# Revit family: M_Valve_Balancing and Control_MEPcontent_Oventrop_Hydrocontrol VFC 10626 DN 200-400 PN16 DIN
name_source: partatom
category: Pipe Accessories
revit_build: Autodesk Revit 2015 (Build: 20140223_1515(x64)
units: mm (PartAtom-declared; Revit-internal decimal feet)

## types (5) — shared parameters
Angle = 60.00°
Angle 2 = 30.00°
Angle 3 = -60.00°
Article Description = Double regulating and commissioning valve
Article Type = Hydrocontrol VFC 10626 DN 200-400 PN16 DIN
Black = Color RGB 35-35-35
Bronze = Color RGB 156-122-90
Content Supplier URL = www.mepcontent.eu
Custom = No
Description = Double regulating and commissioning valve
EMCS Version = 2.0
ETIM Article Class = EC011463
Family Version = 10.14
Hb5 = 10 mm  [stored 0.0328084 ft]
Hlp1 = 56 mm  [stored 0.183727 ft]
IFCExportAs = IfcValveType
IFCExportType = PRESSUREREDUCING
Lgt1 = 2 mm  [stored 0.00656168 ft]
MEPcontent Class = VALVE_BALANCING
Manufacturer = Oventrop
Manufacturer URL = http://www.oventrop.de
Model = Hydrocontrol VFC 10626 DN 200-400 PN16 DIN
Pressure Drop = 0.0 Pa
Product Line = Oventrop
R1 = 9 mm  [stored 0.0295276 ft]
R2 = 10 mm  [stored 0.0328084 ft]
RegulatorRadius = 150 mm
Revit Version = 2015
Steel = Color RGB 140-140-140
URL = www.stabiplan.com
r1 = 2 mm  [stored 0.00656168 ft]
r2 = 3 mm  [stored 0.00984252 ft]

## per-type parameters (varying)
- DN 200: CurDst=67 mm; Dst1=68 mm; DstChk=68 mm; FlangeDiameter=340 mm; GTIN=4026755126174; H=473 mm; Hb1=460 mm; Hb2=290 mm; Hb3=48 mm; Hb4=110 mm; Hb6=218 mm; Height=467 mm; Hlp2=22 mm  [stored 0.0721785 ft]; K=295 mm; L2=67 mm; Length=600 mm; Lgt2=20 mm  [stored 0.0656168 ft]; Lgt3=59 mm; Lgt4=217 mm; Manufacturer Art. No.=1062656; NominalDiameter=200 mm; NominalRadius=100 mm; OuterDiameter=219 mm; Rad1=148 mm; Rad2=170 mm; Rad3=119 mm; Rad4=116 mm; Rad5=156 mm; Rad6=146 mm; Rad7=160 mm; VDst=54 mm; VHth=126 mm
- DN 250: CurDst=81 mm; Dst1=91 mm; DstChk=91 mm; FlangeDiameter=405 mm; GTIN=4026755180190; H=486 mm; Hb1=475 mm; Hb2=292 mm; Hb3=49 mm; Hb4=111 mm; Hb6=220 mm; Height=480 mm; Hlp2=27 mm; K=355 mm; L2=81 mm; Length=730 mm; Lgt2=22 mm  [stored 0.0721785 ft]; Lgt3=68 mm; Lgt4=260 mm; Manufacturer Art. No.=1062657; NominalDiameter=250 mm; NominalRadius=125 mm; OuterDiameter=273 mm; Rad1=178 mm; Rad2=203 mm; Rad3=143 mm; Rad4=140 mm; Rad5=180 mm; Rad6=170 mm; Rad7=184 mm; VDst=63 mm; VHth=150 mm
- DN 300: CurDst=94 mm; Dst1=101 mm; DstChk=101 mm; FlangeDiameter=460 mm; GTIN=4026755180206; H=521 mm; Hb1=515 mm; Hb2=319 mm; Hb3=53 mm; Hb4=121 mm; Hb6=250 mm; Height=515 mm; Hlp2=31 mm; K=410 mm; L2=94 mm; Length=850 mm; Lgt2=23 mm; Lgt3=77 mm; Lgt4=302 mm; Manufacturer Art. No.=1062658; NominalDiameter=300 mm; NominalRadius=150 mm; OuterDiameter=324 mm; Rad1=205 mm; Rad2=230 mm; Rad3=166 mm; Rad4=163 mm; Rad5=203 mm; Rad6=193 mm; Rad7=207 mm; VDst=72 mm; VHth=173 mm
- DN 350: CurDst=108 mm; Dst1=106 mm; DstChk=106 mm; FlangeDiameter=520 mm; GTIN=4026755324570; H=566 mm; Hb1=567 mm; Hb2=357 mm; Hb3=59 mm; Hb4=136 mm; Hb6=292 mm; Height=560 mm; Hlp2=36 mm  [stored 0.11811 ft]; K=470 mm; L2=108 mm; Length=980 mm; Lgt2=25 mm  [stored 0.082021 ft]; Lgt3=86 mm; Lgt4=345 mm; Manufacturer Art. No.=1062659; NominalDiameter=350 mm; NominalRadius=175 mm; OuterDiameter=356 mm; Rad1=235 mm; Rad2=260 mm; Rad3=190 mm; Rad4=187 mm; Rad5=227 mm; Rad6=217 mm; Rad7=231 mm; VDst=81 mm; VHth=197 mm
- DN 400: CurDst=121 mm; Dst1=83 mm; DstChk=83 mm; FlangeDiameter=580 mm; GTIN=4026755324587; H=661 mm; Hb1=677 mm; Hb2=453 mm; Hb3=76 mm; Hb4=172 mm; Hb6=399 mm; Height=655 mm; Hlp2=40 mm  [stored 0.131234 ft]; K=525 mm; L2=121 mm; Length=1100 mm; Lgt2=27 mm; Lgt3=95 mm; Lgt4=387 mm; Manufacturer Art. No.=1062660; NominalDiameter=400 mm; NominalRadius=200 mm; OuterDiameter=407 mm; Rad1=263 mm; Rad2=290 mm; Rad3=213 mm; Rad4=210 mm; Rad5=250 mm; Rad6=240 mm; Rad7=254 mm; VDst=90 mm; VHth=220 mm

note: [stored X ft] marks values corroborated as IEEE doubles in the binary element streams (Revit-internal decimal feet)

## geometry (parser evidence)
native form markers: Blend x2, Sweep x2
no freeform markers — native parametric forms only
